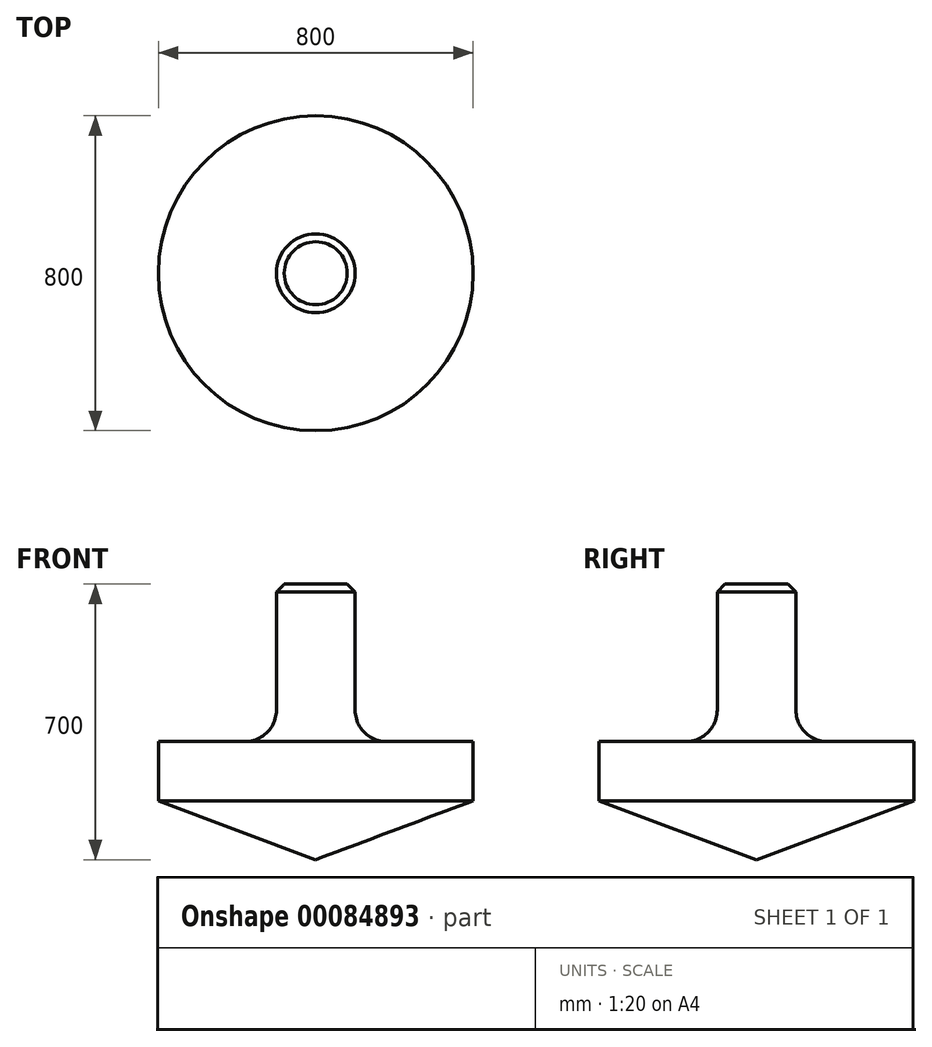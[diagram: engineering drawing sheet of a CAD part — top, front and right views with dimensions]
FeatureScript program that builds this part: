
annotation { "Feature Type Name" : "Feature", "Feature Type Description" : "" }
export const myFeature = defineFeature(function(context is Context, id is Id, definition is map)
    precondition{}
    {
        {
            var Q0;
            Q0=qCreatedBy(makeId("Front.planeOp"),FACE);
            var sketch = newSketch(context, id + "F0", { "sketchPlane" : qUnion([Q0])});
            skLineSegment(sketch, "E0", {"start": v(0, 482.43) * mm, "end": v(0, -217.57) * mm, "construction": true});
            skLineSegment(sketch, "E1", {"start": v(100, 482.43) * mm, "end": v(0, 482.43) * mm});
            skLineSegment(sketch, "E2", {"start": v(180, 82.43) * mm, "end": v(400, 82.43) * mm});
            skLineSegment(sketch, "E3", {"start": v(400, 82.43) * mm, "end": v(400, -67.57) * mm});
            skLineSegment(sketch, "E4", {"start": v(400, -67.57) * mm, "end": v(0, -217.57) * mm});
            skPoint(sketch, "E5.orphan", {"position": v(0, -50.9) * mm});
            skPoint(sketch, "E6.end.orphan", {"position": v(0, -122.07) * mm});
            skLineSegment(sketch, "E7", {"start": v(100, 482.43) * mm, "end": v(100, 162.43) * mm});
            skPoint(sketch, "E8.visualSharp", {"position": v(100, 82.43) * mm});
            skArc(sketch, "E8.filletArc", {"start": v(100, 162.43) * mm, "mid": v(123.43, 105.86) * mm, "end": v(180, 82.43) * mm});
            skLineSegment(sketch, "E9", {"start": v(0, 482.43) * mm, "end": v(0, -217.57) * mm});
            skSolve(sketch);
        }
        {
            var Q0;
            Q0 = qSketchRegion(id + "F0", true);
            var Q1;
            Q1=sQuery(id+"F0.wireOp",EDGE,"E9");
            revolve(context, id + "F1", {"entities" : qUnion([Q0]), "axis" : qUnion([Q1]), "revolveType" : RevolveType.FULL});
        }
        {
            var Q0;
            Q0=makeQuery(id+"F1.opRevolve","SWEPT_EDGE",EDGE,{"disambiguationData":[OSD([sQuery(id+"F0.wireOp",EDGE,"E1"),sQuery(id+"F0.wireOp",EDGE,"E7")])]});
            chamfer(context, id + "F2", {"entities" : qUnion([Q0]), "width" : 20 * mm, "tangentPropagation" : true});
        }
    });
